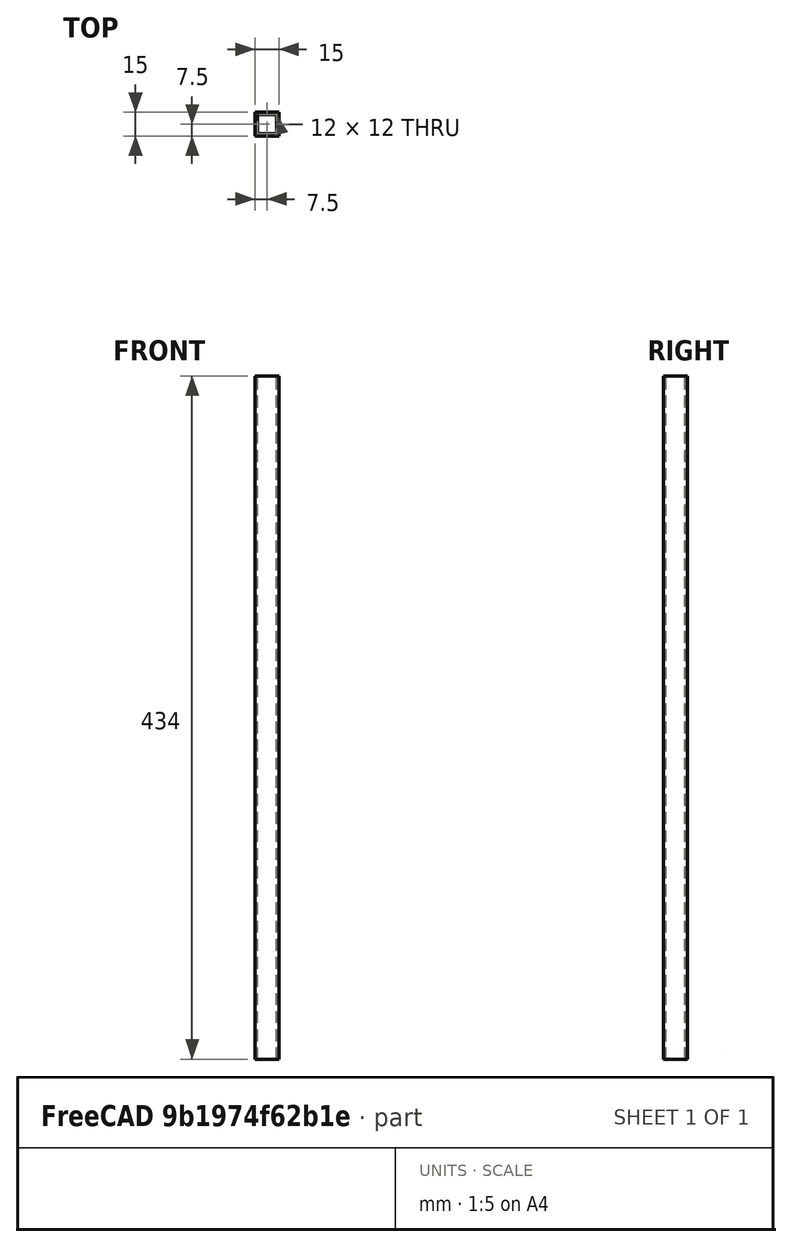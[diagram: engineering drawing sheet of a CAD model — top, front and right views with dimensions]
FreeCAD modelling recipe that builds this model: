
FCSTD DOCUMENT  (FreeCAD 0.16R6698 (Git))
Label: Tube 434
License: All rights reserved
LicenseURL: http://en.wikipedia.org/wiki/All_rights_reserved
objects: Sketcher::SketchObject×1, PartDesign::Pad×1
note: 3 computed .brp shape members not serialized (recipe doc carries the construction recipe); baked Part::Feature solids carry a one-line shape summary decoded from their .brp

FEATURE [Sketcher::SketchObject] Sketch
  sketch-geometry (8):
    g0: LineSegment StartX=-7.5 StartY=7.5 StartZ=0 EndX=7.5 EndY=7.5 EndZ=0
    g1: LineSegment StartX=7.5 StartY=7.5 StartZ=0 EndX=7.5 EndY=-7.5 EndZ=0
    g2: LineSegment StartX=7.5 StartY=-7.5 StartZ=0 EndX=-7.5 EndY=-7.5 EndZ=0
    g3: LineSegment StartX=-7.5 StartY=-7.5 StartZ=0 EndX=-7.5 EndY=7.5 EndZ=0
    g4: LineSegment StartX=-6 StartY=6 StartZ=0 EndX=6 EndY=6 EndZ=0
    g5: LineSegment StartX=6 StartY=6 StartZ=0 EndX=6 EndY=-6 EndZ=0
    g6: LineSegment StartX=6 StartY=-6 StartZ=0 EndX=-6 EndY=-6 EndZ=0
    g7: LineSegment StartX=-6 StartY=-6 StartZ=0 EndX=-6 EndY=6 EndZ=0
  constraints (24):
    c: Coincident(g0,g1)
    c: Coincident(g1,g2)
    c: Coincident(g2,g3)
    c: Coincident(g3,g0)
    c: Horizontal(g0)
    c: Horizontal(g2)
    c: Vertical(g1)
    c: Vertical(g3)
    c: DistanceX(g0,g0) = 15
    c: DistanceY(g1,g1) = 15
    c: DistanceY(g1,g-1) = 7.5
    c: DistanceX(g-1,g0) = 7.5
    c: Coincident(g4,g5)
    c: Coincident(g5,g6)
    c: Coincident(g6,g7)
    c: Coincident(g7,g4)
    c: Horizontal(g4)
    c: Horizontal(g6)
    c: Vertical(g5)
    c: Vertical(g7)
    c: DistanceY(g1,g5) = 1.5
    c: DistanceX(g5,g1) = 1.5
    c: DistanceX(g2,g6) = 1.5
    c: DistanceY(g4,g0) = 1.5
FEATURE [PartDesign::Pad] Pad
  Length = 434
  Length2 = 100
  Sketch = -> Sketch
  Type = 0
